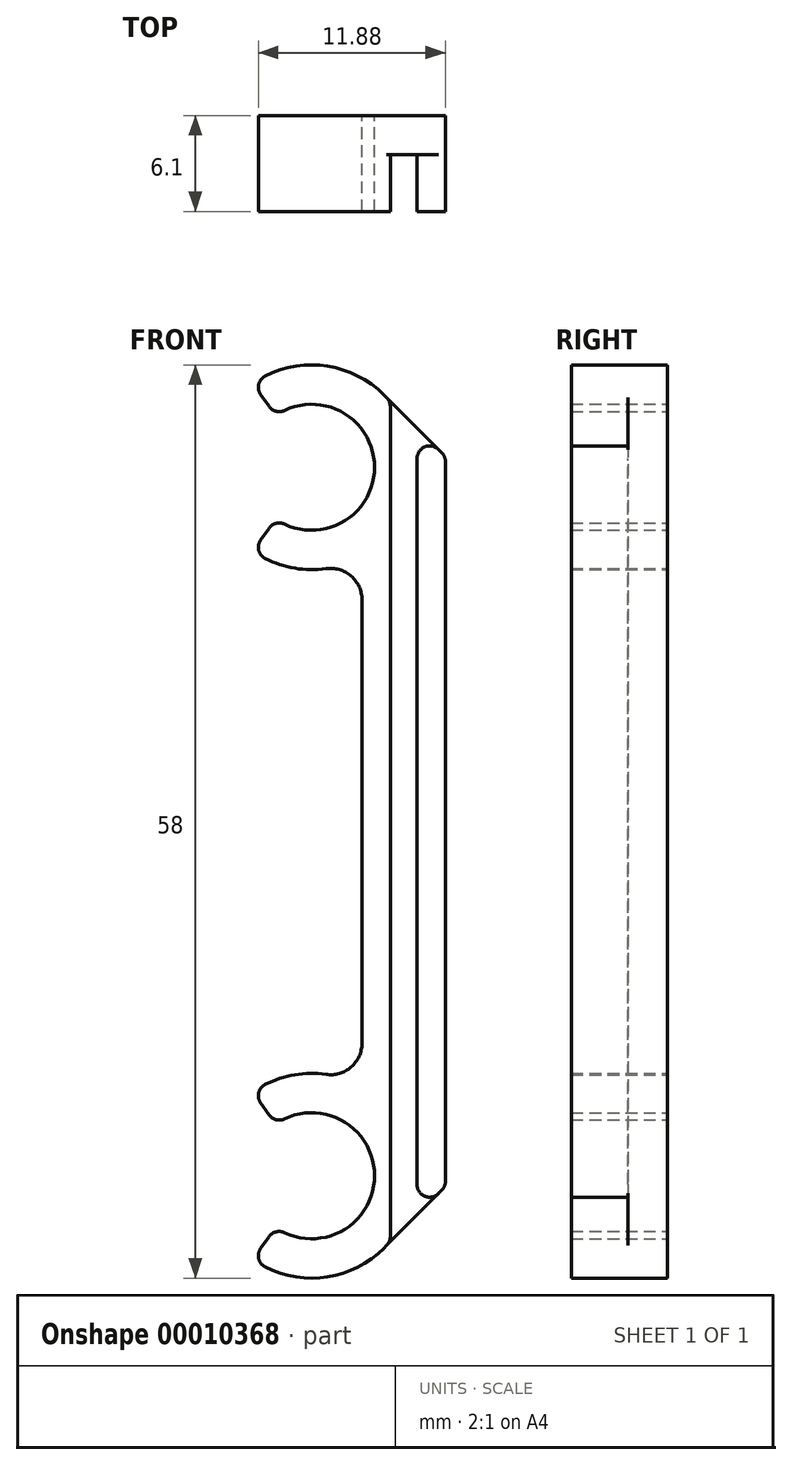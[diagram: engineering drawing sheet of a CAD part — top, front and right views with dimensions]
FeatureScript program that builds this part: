
annotation { "Feature Type Name" : "Feature", "Feature Type Description" : "" }
export const myFeature = defineFeature(function(context is Context, id is Id, definition is map)
    precondition{}
    {
        {
            var Q0;
            Q0=qCreatedBy(makeId("Front.planeOp"),FACE);
            var sketch = newSketch(context, id + "F0", { "sketchPlane" : qUnion([Q0])});
            skArc(sketch, "E0", {"start": v(-2.3, 41.72) * mm, "mid": v(4, 45) * mm, "end": v(-2.3, 48.28) * mm});
            skArc(sketch, "E1", {"start": v(-2.3, -3.28) * mm, "mid": v(4, 0) * mm, "end": v(-2.3, 3.28) * mm});
            skArc(sketch, "E2", {"start": v(0.92, 6.43) * mm, "mid": v(-1.51, 6.32) * mm, "end": v(-3.73, 5.32) * mm});
            skArc(sketch, "E3", {"start": v(4.6, 49.6) * mm, "mid": v(0.57, 51.48) * mm, "end": v(-3.73, 50.32) * mm});
            skLineSegment(sketch, "E4", {"start": v(5, -4.2) * mm, "end": v(5, 49.2) * mm});
            skPoint(sketch, "E5.orphan", {"position": v(4, 0) * mm});
            skLineSegment(sketch, "E6", {"start": v(-2.3, 3.28) * mm, "end": v(-3.73, 5.32) * mm});
            skLineSegment(sketch, "E7", {"start": v(0, 0) * mm, "end": v(-6.5, 0) * mm, "construction": true});
            skLineSegment(sketch, "E8.0.MirrorCS", {"start": v(-2.3, -3.28) * mm, "end": v(-3.73, -5.32) * mm});
            skLineSegment(sketch, "E9", {"start": v(8.5, 22.5) * mm, "end": v(-6.5, 22.5) * mm, "construction": true});
            skArc(sketch, "E10.trimOffspring", {"start": v(-3.73, -5.32) * mm, "mid": v(0.57, -6.48) * mm, "end": v(4.6, -4.6) * mm});
            skLineSegment(sketch, "E11.0.MirrorCS", {"start": v(-2.3, 48.28) * mm, "end": v(-3.73, 50.32) * mm});
            skLineSegment(sketch, "E12.0.MirrorCS", {"start": v(-2.3, 41.72) * mm, "end": v(-3.73, 39.68) * mm});
            skArc(sketch, "E13.trimOffspring", {"start": v(-3.73, 39.68) * mm, "mid": v(-1.51, 38.68) * mm, "end": v(0.92, 38.57) * mm});
            skLineSegment(sketch, "E14", {"start": v(4.6, 49.6) * mm, "end": v(8.5, 45.7) * mm});
            skLineSegment(sketch, "E15.0.MirrorCS", {"start": v(4.6, -4.6) * mm, "end": v(8.5, -0.7) * mm});
            skLineSegment(sketch, "E16.trimOffspring", {"start": v(6.7, 47.5) * mm, "end": v(6.7, -2.5) * mm});
            skPoint(sketch, "E17.visualSharp", {"position": v(8.5, -0.7) * mm});
            skPoint(sketch, "E18.orphan", {"position": v(4, 22.5) * mm});
            skLineSegment(sketch, "E19.0", {"start": v(8.5, 45.7) * mm, "end": v(8.5, -0.7) * mm});
            skLineSegment(sketch, "E20", {"start": v(3.2, 36.59) * mm, "end": v(3.2, 8.41) * mm});
            skArc(sketch, "E21.filletArc", {"start": v(0.92, 6.43) * mm, "mid": v(2.51, 6.9) * mm, "end": v(3.2, 8.41) * mm});
            skArc(sketch, "E22.filletArc", {"start": v(3.2, 36.59) * mm, "mid": v(2.51, 38.1) * mm, "end": v(0.92, 38.57) * mm});
            skSolve(sketch);
        }
        {
            var Q0;
            Q0=makeQuery(id+"F0.imprint","IMPRINT",FACE,{"disambiguationData":[TD([[makeQuery(id+"F0.imprint","IMPRINT",EDGE,{"derivedFrom":sQuery(id+"F0.wireOp",EDGE,"E0")}),-1.0]])]});
            var Q1;
            Q1=makeQuery(id+"F0.imprint","IMPRINT",FACE,{"disambiguationData":[TD([[makeQuery(id+"F0.imprint","IMPRINT",EDGE,{"derivedFrom":sQuery(id+"F0.wireOp",EDGE,"dfa2cc31-a6e8-46c3-b2ce-c2e06a46fc66")}),-1.0]])]});
            var Q2;
            {var subQ1=sQuery(id+"F0.wireOp",EDGE,"1ba8ad5c-b601-476a-9779-88b53e210d94");Q2=makeQuery(id+"F0.imprint","IMPRINT",FACE,{"disambiguationData":[TD([[makeQuery(id+"F0.imprint","IMPRINT",EDGE,{"derivedFrom":subQ1}),1.0]])]});}
            var Q3;
            Q3=makeQuery(id+"F0.imprint","IMPRINT",FACE,{"disambiguationData":[TD([[makeQuery(id+"F0.imprint","IMPRINT",EDGE,{"derivedFrom":sQuery(id+"F0.wireOp",EDGE,"dfa2cc31-a6e8-46c3-b2ce-c2e06a46fc66")}),1.0]])]});
            var Q4;
            {var subQ4=sQuery(id+"F0.wireOp",EDGE,"aa7d58d1-2776-434c-a1b8-937a125aae7e.0.MirrorCS");Q4=makeQuery(id+"F0.imprint","IMPRINT",FACE,{"disambiguationData":[TD([[makeQuery(id+"F0.imprint","IMPRINT",EDGE,{"derivedFrom":subQ4}),-1.0]])]});}
            var Q5;
            {var subQ3=sQuery(id+"F0.wireOp",EDGE,"695c2fa7-dfbd-4be1-8a4d-e9ee8b981d7d");Q5=makeQuery(id+"F0.imprint","IMPRINT",FACE,{"disambiguationData":[TD([[makeQuery(id+"F0.imprint","IMPRINT",EDGE,{"derivedFrom":subQ3}),1.0]])]});}
            var Q6;
            Q6=makeQuery(id+"F0.imprint","IMPRINT",FACE,{"disambiguationData":[TD([[makeQuery(id+"F0.imprint","IMPRINT",EDGE,{"derivedFrom":sQuery(id+"F0.wireOp",EDGE,"2eeb60b7-0f88-4b5b-8cb8-60df6ddea03d")}),-1.0]])]});
            var Q7;
            {var subQ2=sQuery(id+"F0.wireOp",EDGE,"E4");Q7=makeQuery(id+"F0.imprint","IMPRINT",FACE,{"disambiguationData":[TD([[makeQuery(id+"F0.imprint","IMPRINT",EDGE,{"derivedFrom":subQ2}),-1.0]])]});}
            var Q8;
            {var subQ1=sQuery(id+"F0.wireOp",EDGE,"E16.trimOffspring");Q8=makeQuery(id+"F0.imprint","IMPRINT",FACE,{"disambiguationData":[TD([[makeQuery(id+"F0.imprint","IMPRINT",EDGE,{"derivedFrom":subQ1}),1.0]])]});}
            extrude(context, id + "F1", {"entities" : qUnion([Q0, Q1, Q2, Q3, Q4, Q5, Q6, Q7, Q8]), "depth" : 2.5 * mm});
        }
        {
            var Q0;
            Q0=makeQuery(id+"F0.imprint","IMPRINT",FACE,{"disambiguationData":[TD([[makeQuery(id+"F0.imprint","IMPRINT",EDGE,{"derivedFrom":sQuery(id+"F0.wireOp",EDGE,"dfa2cc31-a6e8-46c3-b2ce-c2e06a46fc66")}),1.0]])]});
            var Q1;
            Q1=makeQuery(id+"F0.imprint","IMPRINT",FACE,{"disambiguationData":[TD([[makeQuery(id+"F0.imprint","IMPRINT",EDGE,{"derivedFrom":sQuery(id+"F0.wireOp",EDGE,"E0")}),-1.0]])]});
            var Q2;
            {var subQ4=sQuery(id+"F0.wireOp",EDGE,"aa7d58d1-2776-434c-a1b8-937a125aae7e.0.MirrorCS");Q2=makeQuery(id+"F0.imprint","IMPRINT",FACE,{"disambiguationData":[TD([[makeQuery(id+"F0.imprint","IMPRINT",EDGE,{"derivedFrom":subQ4}),-1.0]])]});}
            var Q3;
            Q3=makeQuery(id+"F0.imprint","IMPRINT",FACE,{"disambiguationData":[TD([[makeQuery(id+"F0.imprint","IMPRINT",EDGE,{"derivedFrom":sQuery(id+"F0.wireOp",EDGE,"2eeb60b7-0f88-4b5b-8cb8-60df6ddea03d")}),-1.0]])]});
            var Q4;
            {var subQ1=sQuery(id+"F0.wireOp",EDGE,"E16.trimOffspring");Q4=makeQuery(id+"F0.imprint","IMPRINT",FACE,{"disambiguationData":[TD([[makeQuery(id+"F0.imprint","IMPRINT",EDGE,{"derivedFrom":subQ1}),1.0]])]});}
            extrude(context, id + "F2", {"entities" : qUnion([Q0, Q1, Q2, Q3, Q4]), "operationType" : NewBodyOperationType.ADD, "depth" : (3.6 + 2.5) * mm});
        }
        {
            var Q0;
            {var subQ0=sQuery(id+"F0.wireOp",EDGE,"E3");var subQ1=sQuery(id+"F0.wireOp",EDGE,"E14");var subQ2=sQuery(id+"F0.wireOp",EDGE,"E19.0");Q0=qUnion([makeQuery(id+"F2.boolean.opBoolean","MERGE",EDGE,{"derivedFrom":[makeQuery(id+"F1.opExtrude","SWEPT_EDGE",EDGE,{"disambiguationData":[OSD([subQ0,subQ1])]}),makeQuery(id+"F2.opExtrude","SWEPT_EDGE",EDGE,{"disambiguationData":[OSD([subQ0,subQ1])]})]}),makeQuery(id+"F2.boolean.opBoolean","MERGE",EDGE,{"derivedFrom":[makeQuery(id+"F1.opExtrude","SWEPT_EDGE",EDGE,{"disambiguationData":[OSD([subQ1,subQ2])]}),makeQuery(id+"F2.opExtrude","SWEPT_EDGE",EDGE,{"disambiguationData":[OSD([subQ1,subQ2])]})]}),makeQuery(id+"F2.opExtrude","SWEPT_EDGE",EDGE,{"disambiguationData":[OSD([sQuery(id+"F0.wireOp",EDGE,"E4"),subQ1])]}),makeQuery(id+"F2.opExtrude","SWEPT_EDGE",EDGE,{"disambiguationData":[OSD([subQ1,sQuery(id+"F0.wireOp",EDGE,"E16.trimOffspring")])]})]);}
            var Q1;
            Q1=makeQuery(id+"F2.opExtrude","SWEPT_EDGE",EDGE,{"disambiguationData":[OSD([sQuery(id+"F0.wireOp",EDGE,"E15.0.MirrorCS"),sQuery(id+"F0.wireOp",EDGE,"E16.trimOffspring")])]});
            var Q2;
            {var subQ0=sQuery(id+"F0.wireOp",EDGE,"E3");var subQ1=sQuery(id+"F0.wireOp",EDGE,"E11.0.MirrorCS");Q2=makeQuery(id+"F2.boolean.opBoolean","MERGE",EDGE,{"derivedFrom":[makeQuery(id+"F1.opExtrude","SWEPT_EDGE",EDGE,{"disambiguationData":[OSD([subQ0,subQ1])]}),makeQuery(id+"F2.opExtrude","SWEPT_EDGE",EDGE,{"disambiguationData":[OSD([subQ0,subQ1])]})]});}
            var Q3;
            {var subQ0=sQuery(id+"F0.wireOp",EDGE,"E0");var subQ1=sQuery(id+"F0.wireOp",EDGE,"E11.0.MirrorCS");Q3=makeQuery(id+"F2.boolean.opBoolean","MERGE",EDGE,{"derivedFrom":[makeQuery(id+"F1.opExtrude","SWEPT_EDGE",EDGE,{"disambiguationData":[OSD([subQ0,subQ1])]}),makeQuery(id+"F2.opExtrude","SWEPT_EDGE",EDGE,{"disambiguationData":[OSD([subQ0,subQ1])]})]});}
            var Q4;
            {var subQ0=sQuery(id+"F0.wireOp",EDGE,"E0");var subQ1=sQuery(id+"F0.wireOp",EDGE,"E12.0.MirrorCS");Q4=makeQuery(id+"F2.boolean.opBoolean","MERGE",EDGE,{"derivedFrom":[makeQuery(id+"F1.opExtrude","SWEPT_EDGE",EDGE,{"disambiguationData":[OSD([subQ0,subQ1])]}),makeQuery(id+"F2.opExtrude","SWEPT_EDGE",EDGE,{"disambiguationData":[OSD([subQ0,subQ1])]})]});}
            var Q5;
            {var subQ0=sQuery(id+"F0.wireOp",EDGE,"E12.0.MirrorCS");var subQ1=sQuery(id+"F0.wireOp",EDGE,"E13.trimOffspring");Q5=makeQuery(id+"F2.boolean.opBoolean","MERGE",EDGE,{"derivedFrom":[makeQuery(id+"F1.opExtrude","SWEPT_EDGE",EDGE,{"disambiguationData":[OSD([subQ0,subQ1])]}),makeQuery(id+"F2.opExtrude","SWEPT_EDGE",EDGE,{"disambiguationData":[OSD([subQ0,subQ1])]})]});}
            var Q6;
            {var subQ0=sQuery(id+"F0.wireOp",EDGE,"E2");var subQ1=sQuery(id+"F0.wireOp",EDGE,"E6");Q6=makeQuery(id+"F2.boolean.opBoolean","MERGE",EDGE,{"derivedFrom":[makeQuery(id+"F1.opExtrude","SWEPT_EDGE",EDGE,{"disambiguationData":[OSD([subQ0,subQ1])]}),makeQuery(id+"F2.opExtrude","SWEPT_EDGE",EDGE,{"disambiguationData":[OSD([subQ0,subQ1])]})]});}
            var Q7;
            {var subQ0=sQuery(id+"F0.wireOp",EDGE,"E1");var subQ1=sQuery(id+"F0.wireOp",EDGE,"E6");Q7=makeQuery(id+"F2.boolean.opBoolean","MERGE",EDGE,{"derivedFrom":[makeQuery(id+"F1.opExtrude","SWEPT_EDGE",EDGE,{"disambiguationData":[OSD([subQ0,subQ1])]}),makeQuery(id+"F2.opExtrude","SWEPT_EDGE",EDGE,{"disambiguationData":[OSD([subQ0,subQ1])]})]});}
            var Q8;
            {var subQ0=sQuery(id+"F0.wireOp",EDGE,"E1");var subQ1=sQuery(id+"F0.wireOp",EDGE,"E8.0.MirrorCS");Q8=makeQuery(id+"F2.boolean.opBoolean","MERGE",EDGE,{"derivedFrom":[makeQuery(id+"F1.opExtrude","SWEPT_EDGE",EDGE,{"disambiguationData":[OSD([subQ0,subQ1])]}),makeQuery(id+"F2.opExtrude","SWEPT_EDGE",EDGE,{"disambiguationData":[OSD([subQ0,subQ1])]})]});}
            var Q9;
            {var subQ0=sQuery(id+"F0.wireOp",EDGE,"E8.0.MirrorCS");var subQ1=sQuery(id+"F0.wireOp",EDGE,"E10.trimOffspring");Q9=makeQuery(id+"F2.boolean.opBoolean","MERGE",EDGE,{"derivedFrom":[makeQuery(id+"F1.opExtrude","SWEPT_EDGE",EDGE,{"disambiguationData":[OSD([subQ0,subQ1])]}),makeQuery(id+"F2.opExtrude","SWEPT_EDGE",EDGE,{"disambiguationData":[OSD([subQ0,subQ1])]})]});}
            var Q10;
            Q10=makeQuery(id+"F2.opExtrude","SWEPT_EDGE",EDGE,{"disambiguationData":[OSD([sQuery(id+"F0.wireOp",EDGE,"E4"),sQuery(id+"F0.wireOp",EDGE,"E15.0.MirrorCS")])]});
            var Q11;
            {var subQ0=sQuery(id+"F0.wireOp",EDGE,"E15.0.MirrorCS");var subQ1=sQuery(id+"F0.wireOp",EDGE,"E19.0");Q11=makeQuery(id+"F2.boolean.opBoolean","MERGE",EDGE,{"derivedFrom":[makeQuery(id+"F1.opExtrude","SWEPT_EDGE",EDGE,{"disambiguationData":[OSD([subQ0,subQ1])]}),makeQuery(id+"F2.opExtrude","SWEPT_EDGE",EDGE,{"disambiguationData":[OSD([subQ0,subQ1])]})]});}
            fillet(context, id + "F3", {"entities" : qUnion([Q0, Q1, Q2, Q3, Q4, Q5, Q6, Q7, Q8, Q9, Q10, Q11]), "radius" : 0.8 * mm, "tangentPropagation" : true, "allowEdgeOverflow" : false});
        }
    });
